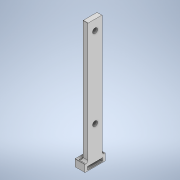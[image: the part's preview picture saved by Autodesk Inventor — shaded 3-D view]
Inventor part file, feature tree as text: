
AUTODESK INVENTOR PART (.ipt)
format: ipt  version: 2021.4 (Build 254397000, 397)  size: 167,936 bytes
history: native  units: mm
features: sketch x5, extrude x4, fillet x2, other x1, hole x1
ambient origin geometry x8: Origin, YZ Plane, XZ Plane, XY Plane, X Axis, Y Axis, Z Axis, Center Point
bodies: Body1 (feature_tree)
feature tree (13):
  other  "ソリッド1"
  extrude  "押し出し1"  Depth=10.0mm
  extrude  "押し出し2"  Depth=20.0mm
  extrude  "押し出し3"  Depth=6.0mm TaperAngle=0.0deg
  extrude  "押し出し4"  Depth=15.0mm
  fillet  "フィレット1"  Radius=3.0mm
  fillet  "フィレット2"  Radius=10.0mm
  hole  "穴1"  [1 undecoded]
  sketch  "スケッチ1"
  sketch  "スケッチ2"
  sketch  "スケッチ3"
  sketch  "スケッチ4"
  sketch  "スケッチ5"
note: 1 required parameter value undecoded (feature->parameter linkage not recoverable at this tier; creation-order binding heuristic only, values carry confidence <= 0.55)
